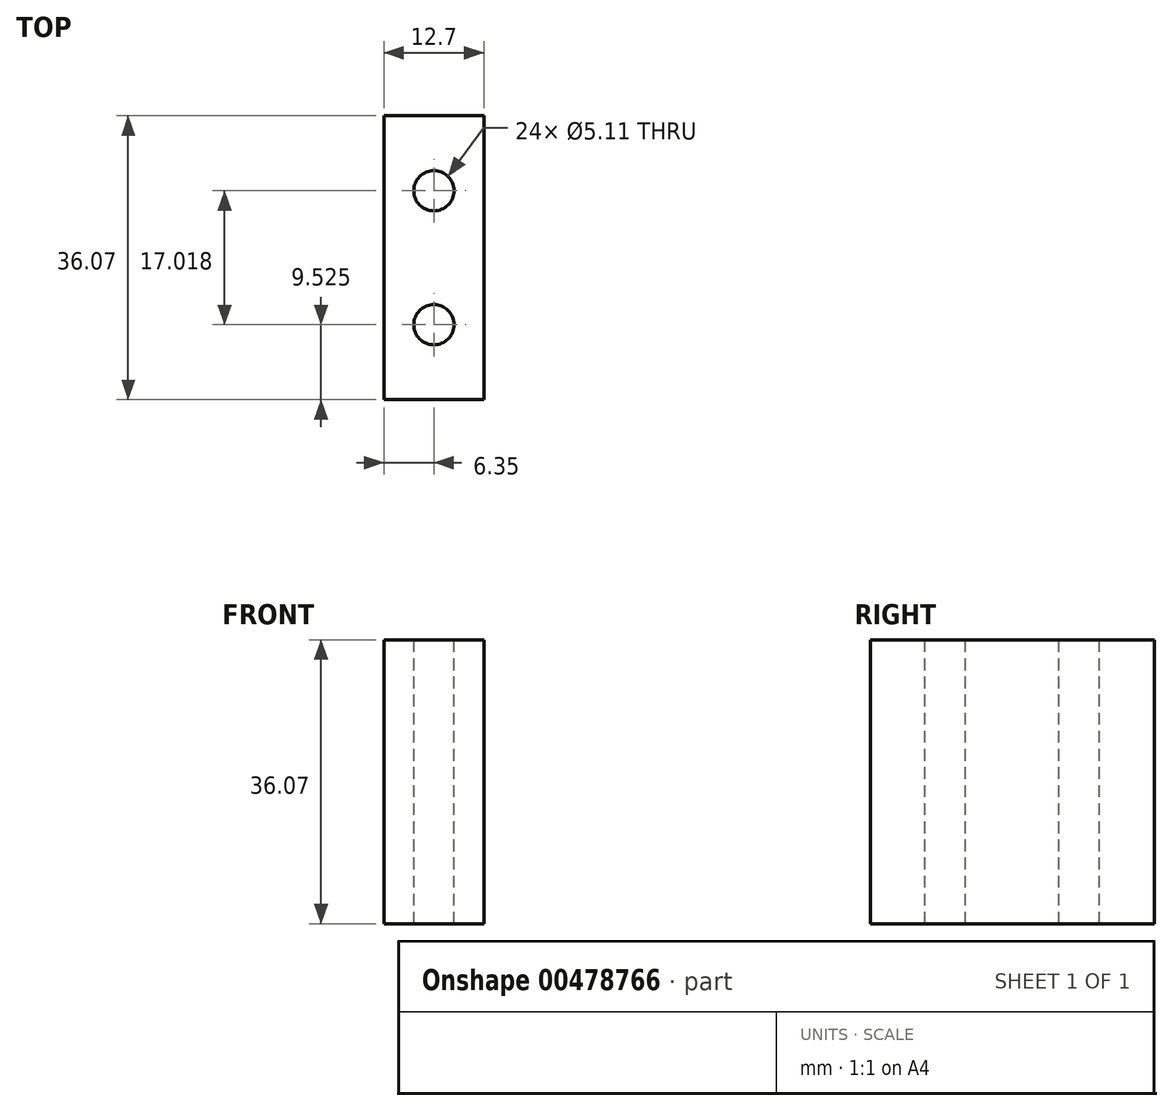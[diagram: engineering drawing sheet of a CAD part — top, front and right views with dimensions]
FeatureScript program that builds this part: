
annotation { "Feature Type Name" : "Feature", "Feature Type Description" : "" }
export const myFeature = defineFeature(function(context is Context, id is Id, definition is map)
    precondition{}
    {
        {
            var Q0;
            Q0=qCreatedBy(makeId("Top.planeOp"),FACE);
            var sketch = newSketch(context, id + "F0", { "sketchPlane" : qUnion([Q0])});
            skLineSegment(sketch, "E0.bottom", {"start": v(0, 0) * mm, "end": v(12.7, 0) * mm});
            skLineSegment(sketch, "E0.top", {"start": v(0, 36.07) * mm, "end": v(12.7, 36.07) * mm});
            skLineSegment(sketch, "E0.left", {"start": v(0, 0) * mm, "end": v(0, 36.07) * mm});
            skLineSegment(sketch, "E0.right", {"start": v(12.7, 0) * mm, "end": v(12.7, 36.07) * mm});
            skSolve(sketch);
        }
        {
            var Q0;
            Q0 = qSketchRegion(id + "F0", true);
            extrude(context, id + "F1", {"entities" : qUnion([Q0]), "oppositeDirection" : true, "depth" : 36.07 * mm});
        }
        {
            var Q0;
            Q0=makeQuery(id+"F1.opExtrude","CAP_FACE",FACE,{"disambiguationData":[OSD([sQuery(id+"F0.wireOp",EDGE,"E0.bottom"),sQuery(id+"F0.wireOp",EDGE,"E0.top"),sQuery(id+"F0.wireOp",EDGE,"E0.left"),sQuery(id+"F0.wireOp",EDGE,"E0.right")])],"isStart":true});
            var sketch = newSketch(context, id + "F2", { "sketchPlane" : qUnion([Q0])});
            skPoint(sketch, "E1", {"position": v(6.35, 26.54) * mm});
            skPoint(sketch, "E2", {"position": v(6.35, 9.53) * mm});
            skLineSegment(sketch, "E3", {"start": v(6.35, 36.07) * mm, "end": v(6.35, 0) * mm, "construction": true});
            skSolve(sketch);
        }
        {
            var Q0;
            Q0=sQuery(id+"F2.wireOp",VERTEX,"E2");
            var Q1;
            Q1=sQuery(id+"F2.wireOp",VERTEX,"E1");
            var Q2;
            Q2=makeQuery(id+"F1.opExtrude","SWEPT_BODY",BODY,{"disambiguationData":[OSD([sQuery(id+"F0.wireOp",EDGE,"E0.bottom"),sQuery(id+"F0.wireOp",EDGE,"E0.top"),sQuery(id+"F0.wireOp",EDGE,"E0.left"),sQuery(id+"F0.wireOp",EDGE,"E0.right")])]});
            hole(context, id + "F3", {"style" : HoleStyle.SIMPLE, "endStyle" : HoleEndStyle.THROUGH, "standardTappedOrClearance" : lookupTablePath({ "standard" : "ANSI", "engagement" : "75%", "pitch" : "20 tpi", "size" : "1/4", "type" : "Tapped" }), "standardBlindInLast" : lookupTablePath({ "standard" : "ANSI", "engagement" : "75%", "pitch" : "20 tpi", "size" : "1/4", "type" : "Tapped" }), "holeDiameter" : 5.1 * mm, "showTappedDepth" : true, "tappedDepth" : 12.7 * mm, "tapClearance" : 3, "locations" : qUnion([Q0, Q1]), "scope" : qUnion([Q2]), "majorDiameter" : 6.35 * mm});
        }
    });
